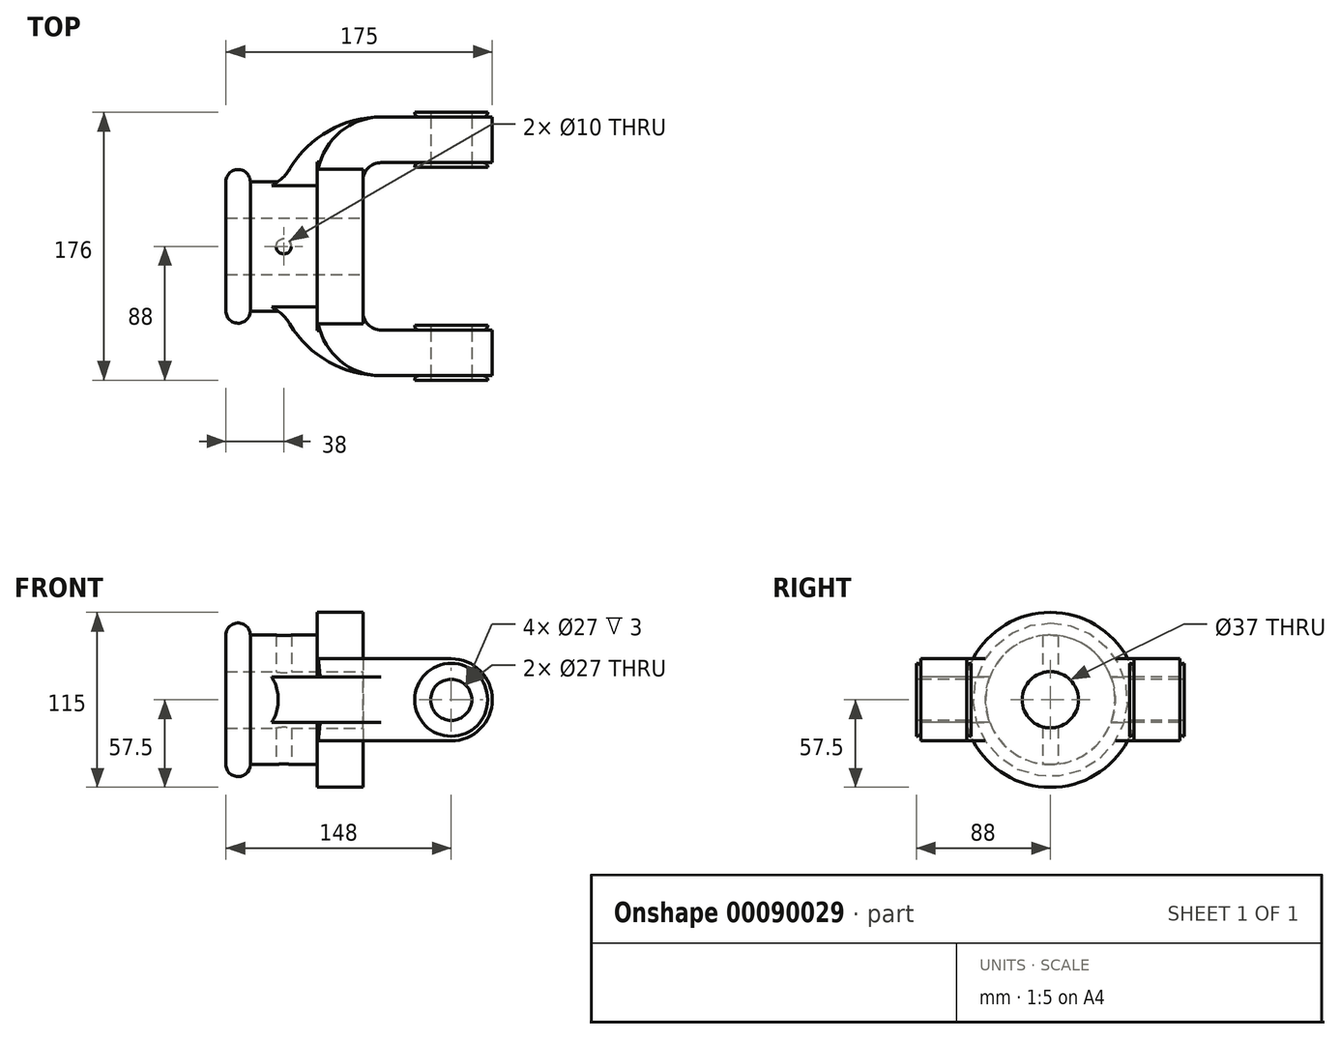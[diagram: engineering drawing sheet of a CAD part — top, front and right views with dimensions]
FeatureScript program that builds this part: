
annotation { "Feature Type Name" : "Feature", "Feature Type Description" : "" }
export const myFeature = defineFeature(function(context is Context, id is Id, definition is map)
    precondition{}
    {
        {
            var Q0;
            Q0=qCreatedBy(makeId("Top.planeOp"),FACE);
            var sketch = newSketch(context, id + "F0", { "sketchPlane" : qUnion([Q0])});
            skLineSegment(sketch, "E0", {"start": v(-90, 0) * mm, "end": v(85, 0) * mm, "construction": true});
            skLineSegment(sketch, "E1", {"start": v(0, 0) * mm, "end": v(0, 43) * mm});
            skLineSegment(sketch, "E2", {"start": v(12, 55) * mm, "end": v(85, 55) * mm});
            skLineSegment(sketch, "E3", {"start": v(85, 55) * mm, "end": v(85, 85) * mm});
            skPoint(sketch, "E4.visualSharp", {"position": v(0, 55) * mm});
            skArc(sketch, "E4.filletArc", {"start": v(12, 55) * mm, "mid": v(3.51, 51.49) * mm, "end": v(0, 43) * mm});
            skLineSegment(sketch, "E5.0", {"start": v(12, 85) * mm, "end": v(85, 85) * mm});
            skArc(sketch, "E5.1", {"start": v(12, 85) * mm, "mid": v(-17.7, 72.7) * mm, "end": v(-30, 43) * mm});
            skLineSegment(sketch, "E5.2", {"start": v(-30, 0) * mm, "end": v(-30, 43) * mm});
            skLineSegment(sketch, "E6.MirrorCS", {"start": v(0, 0) * mm, "end": v(0, -43) * mm});
            skLineSegment(sketch, "E7.MirrorCS", {"start": v(-30, 0) * mm, "end": v(-30, -43) * mm});
            skArc(sketch, "E8.MirrorCS", {"start": v(12, -85) * mm, "mid": v(-17.7, -72.7) * mm, "end": v(-30, -43) * mm});
            skArc(sketch, "E9.MirrorCS", {"start": v(12, -55) * mm, "mid": v(3.51, -51.49) * mm, "end": v(0, -43) * mm});
            skLineSegment(sketch, "E10.MirrorCS", {"start": v(12, -55) * mm, "end": v(85, -55) * mm});
            skLineSegment(sketch, "E11.MirrorCS", {"start": v(12, -85) * mm, "end": v(85, -85) * mm});
            skLineSegment(sketch, "E12.MirrorCS", {"start": v(85, -55) * mm, "end": v(85, -85) * mm});
            skArc(sketch, "E13", {"start": v(12, 85) * mm, "mid": v(-22.47, 75.93) * mm, "end": v(-48, 51.06) * mm});
            skLineSegment(sketch, "E14", {"start": v(-74, 42.5) * mm, "end": v(-30, 42.5) * mm});
            skLineSegment(sketch, "E15", {"start": v(-90, 42.5) * mm, "end": v(-90, 0) * mm});
            skArc(sketch, "E16", {"start": v(-74, 42.5) * mm, "mid": v(-82, 50.5) * mm, "end": v(-90, 42.5) * mm});
            skArc(sketch, "E17", {"start": v(-60, 39.83) * mm, "mid": v(-53.22, 44.6) * mm, "end": v(-48, 51.06) * mm});
            skLineSegment(sketch, "E18", {"start": v(-90, 0) * mm, "end": v(-30, 0) * mm});
            skArc(sketch, "E19.MirrorCS", {"start": v(12, -85) * mm, "mid": v(-22.47, -75.93) * mm, "end": v(-48, -51.06) * mm});
            skArc(sketch, "E20.MirrorCS", {"start": v(-60, -39.83) * mm, "mid": v(-53.22, -44.6) * mm, "end": v(-48, -51.06) * mm});
            skLineSegment(sketch, "E21", {"start": v(-60, 39.83) * mm, "end": v(-60, -39.83) * mm});
            skSolve(sketch);
        }
        {
            var Q0;
            {var subQ1=sQuery(id+"F0.wireOp",EDGE,"E7.MirrorCS");Q0=makeQuery(id+"F0.imprint","IMPRINT",FACE,{"disambiguationData":[TD([[makeQuery(id+"F0.imprint","IMPRINT",EDGE,{"derivedFrom":subQ1}),-1.0]])]});}
            var Q1;
            {var subQ1=sQuery(id+"F0.wireOp",EDGE,"E5.2");var subQ5=sQuery(id+"F0.wireOp",EDGE,"E14");var subQ6=makeQuery(id+"F0.imprint","INTERSECT",VERTEX,{"derivedFrom":[subQ1,subQ5]});Q1=makeQuery(id+"F0.imprint","IMPRINT",FACE,{"disambiguationData":[TD([[makeQuery(id+"F0.imprint","IMPRINT",EDGE,{"disambiguationData":[TD([[subQ6,1.0]])],"derivedFrom":subQ5}),-1.0]])]});}
            var Q2;
            {var subQ6=sQuery(id+"F0.wireOp",EDGE,"E5.1");Q2=makeQuery(id+"F0.imprint","IMPRINT",FACE,{"disambiguationData":[TD([[makeQuery(id+"F0.imprint","IMPRINT",EDGE,{"derivedFrom":subQ6}),-1.0]])]});}
            extrude(context, id + "F1", {"entities" : qUnion([Q0, Q1, Q2]), "depth" : 30 * mm, "symmetric" : true});
        }
        {
            var Q0;
            {var subQ6=sQuery(id+"F0.wireOp",EDGE,"E15");Q0=makeQuery(id+"F0.imprint","IMPRINT",FACE,{"disambiguationData":[TD([[makeQuery(id+"F0.imprint","IMPRINT",EDGE,{"derivedFrom":subQ6}),1.0]])]});}
            var Q1;
            {var subQ1=sQuery(id+"F0.wireOp",EDGE,"E5.2");var subQ5=sQuery(id+"F0.wireOp",EDGE,"E14");var subQ6=makeQuery(id+"F0.imprint","INTERSECT",VERTEX,{"derivedFrom":[subQ1,subQ5]});Q1=makeQuery(id+"F0.imprint","IMPRINT",FACE,{"disambiguationData":[TD([[makeQuery(id+"F0.imprint","IMPRINT",EDGE,{"disambiguationData":[TD([[subQ6,1.0]])],"derivedFrom":subQ5}),-1.0]])]});}
            var Q2;
            Q2=sQuery(id+"F0.wireOp",EDGE,"E18");
            revolve(context, id + "F2", {"operationType" : NewBodyOperationType.ADD, "entities" : qUnion([Q0, Q1]), "axis" : qUnion([Q2]), "revolveType" : RevolveType.FULL});
        }
        {
            var Q0;
            Q0=makeQuery(id+"F0.imprint","IMPRINT",FACE,{"disambiguationData":[TD([[makeQuery(id+"F0.imprint","IMPRINT",EDGE,{"derivedFrom":sQuery(id+"F0.wireOp",EDGE,"E1")}),1.0]])]});
            extrude(context, id + "F3", {"entities" : qUnion([Q0]), "operationType" : NewBodyOperationType.ADD, "depth" : 54 * mm, "symmetric" : true});
        }
        {
            var Q0;
            Q0=qCreatedBy(makeId("Right.planeOp"),FACE);
            var sketch = newSketch(context, id + "F4", { "sketchPlane" : qUnion([Q0])});
            skCircle(sketch, "E22", {"center": v(0, 0) * mm, "radius": 57.5 * mm});
            skSolve(sketch);
        }
        {
            var Q0;
            Q0=makeQuery(id+"F4.imprint","IMPRINT",FACE,{"disambiguationData":[TD([[makeQuery(id+"F4.imprint","IMPRINT",EDGE,{"derivedFrom":sQuery(id+"F4.wireOp",EDGE,"E22")}),1.0]])]});
            extrude(context, id + "F5", {"entities" : qUnion([Q0]), "operationType" : NewBodyOperationType.ADD, "oppositeDirection" : true, "depth" : 30 * mm});
        }
        {
            var Q0;
            Q0=makeQuery(id+"F3.opExtrude","CAP_EDGE",EDGE,{"disambiguationData":[OSD([sQuery(id+"F0.wireOp",EDGE,"E12.MirrorCS")])],"isStart":false});
            var Q1;
            Q1=makeQuery(id+"F3.opExtrude","CAP_EDGE",EDGE,{"disambiguationData":[OSD([sQuery(id+"F0.wireOp",EDGE,"E12.MirrorCS")])],"isStart":true});
            var Q2;
            Q2=makeQuery(id+"F3.opExtrude","CAP_EDGE",EDGE,{"disambiguationData":[OSD([sQuery(id+"F0.wireOp",EDGE,"E3")])],"isStart":false});
            var Q3;
            Q3=makeQuery(id+"F3.opExtrude","CAP_EDGE",EDGE,{"disambiguationData":[OSD([sQuery(id+"F0.wireOp",EDGE,"E3")])],"isStart":true});
            fillet(context, id + "F6", {"entities" : qUnion([Q0, Q1, Q2, Q3]), "radius" : 27 * mm, "tangentPropagation" : true, "allowEdgeOverflow" : false});
        }
        {
            var Q0;
            Q0=makeQuery(id+"F3.opExtrude","SWEPT_FACE",FACE,{"disambiguationData":[OSD([sQuery(id+"F0.wireOp",EDGE,"E11.MirrorCS")])]});
            var sketch = newSketch(context, id + "F7", { "sketchPlane" : qUnion([Q0])});
            skCircle(sketch, "E23", {"center": v(58, 0) * mm, "radius": 24 * mm});
            skSolve(sketch);
        }
        {
            var Q0;
            Q0=makeQuery(id+"F7.imprint","IMPRINT",FACE,{"disambiguationData":[TD([[makeQuery(id+"F7.imprint","IMPRINT",EDGE,{"derivedFrom":sQuery(id+"F7.wireOp",EDGE,"E23")}),1.0]])]});
            extrude(context, id + "F8", {"entities" : qUnion([Q0]), "depth" : 3 * mm});
        }
        {
            var Q0;
            Q0=makeQuery(id+"F8.opExtrude","SWEPT_BODY",BODY,{"disambiguationData":[OSD([sQuery(id+"F7.wireOp",EDGE,"E23")])]});
            var Q1;
            Q1=makeQuery(id+"F3.opExtrude","SWEPT_FACE",FACE,{"disambiguationData":[OSD([sQuery(id+"F0.wireOp",EDGE,"E10.MirrorCS")])]});
            transform(context, id + "F9", {"entities" : qUnion([Q0]), "transformType" : TransformType.TRANSLATION_DISTANCE, "transformDirection" : qUnion([Q1]), "distance" : 33 * mm, "makeCopy" : true});
        }
        {
            var Q0;
            Q0=makeQuery(id+"F8.opExtrude","SWEPT_BODY",BODY,{"disambiguationData":[OSD([sQuery(id+"F7.wireOp",EDGE,"E23")])]});
            var Q1;
            Q1=makeQuery(id+"F9.opPattern","COPY",BODY,{"derivedFrom":makeQuery(id+"F8.opExtrude","SWEPT_BODY",BODY,{"disambiguationData":[OSD([sQuery(id+"F7.wireOp",EDGE,"E23")])]}),"instanceName":"1"});
            var Q2;
            Q2=makeQuery(id+"F3.opExtrude","SWEPT_FACE",FACE,{"disambiguationData":[OSD([sQuery(id+"F0.wireOp",EDGE,"E5.0")])]});
            transform(context, id + "F10", {"entities" : qUnion([Q0, Q1]), "transformType" : TransformType.TRANSLATION_DISTANCE, "transformDirection" : qUnion([Q2]), "distance" : 140 * mm, "makeCopy" : true});
        }
        {
            var Q0;
            Q0=qCreatedBy(makeId("Front.planeOp"),FACE);
            var sketch = newSketch(context, id + "F11", { "sketchPlane" : qUnion([Q0])});
            skCircle(sketch, "E24", {"center": v(58, 0) * mm, "radius": 13.5 * mm});
            skSolve(sketch);
        }
        {
            var Q0;
            Q0=makeQuery(id+"F11.imprint","IMPRINT",FACE,{"disambiguationData":[TD([[makeQuery(id+"F11.imprint","IMPRINT",EDGE,{"derivedFrom":sQuery(id+"F11.wireOp",EDGE,"E24")}),1.0]])]});
            extrude(context, id + "F12", {"entities" : qUnion([Q0]), "operationType" : NewBodyOperationType.REMOVE, "oppositeDirection" : true, "depth" : 185 * mm, "symmetric" : true});
        }
        {
            var Q0;
            Q0=qCreatedBy(makeId("Right.planeOp"),FACE);
            var sketch = newSketch(context, id + "F13", { "sketchPlane" : qUnion([Q0])});
            skCircle(sketch, "E25", {"center": v(0, 0) * mm, "radius": 18.5 * mm});
            skSolve(sketch);
        }
        {
            var Q0;
            Q0=makeQuery(id+"F13.imprint","IMPRINT",FACE,{"disambiguationData":[TD([[makeQuery(id+"F13.imprint","IMPRINT",EDGE,{"derivedFrom":sQuery(id+"F13.wireOp",EDGE,"E25")}),1.0]])]});
            extrude(context, id + "F14", {"entities" : qUnion([Q0]), "operationType" : NewBodyOperationType.REMOVE, "endBound" : BoundingType.UP_TO_NEXT, "oppositeDirection" : true, "depth" : 25 * mm});
        }
        {
            var Q0;
            Q0=makeQuery(id+"F8.opExtrude","CAP_EDGE",EDGE,{"disambiguationData":[OSD([sQuery(id+"F7.wireOp",EDGE,"E23")])],"isStart":true});
            var Q1;
            Q1=makeQuery(id+"F10.opPattern","COPY",EDGE,{"derivedFrom":makeQuery(id+"F8.opExtrude","CAP_EDGE",EDGE,{"disambiguationData":[OSD([sQuery(id+"F7.wireOp",EDGE,"E23")])],"isStart":true}),"instanceName":"1"});
            var Q2;
            Q2=makeQuery(id+"F9.opPattern","COPY",EDGE,{"derivedFrom":makeQuery(id+"F8.opExtrude","CAP_EDGE",EDGE,{"disambiguationData":[OSD([sQuery(id+"F7.wireOp",EDGE,"E23")])],"isStart":false}),"instanceName":"1"});
            var Q3;
            Q3=makeQuery(id+"F10.opPattern","COPY",EDGE,{"derivedFrom":makeQuery(id+"F9.opPattern","COPY",EDGE,{"derivedFrom":makeQuery(id+"F8.opExtrude","CAP_EDGE",EDGE,{"disambiguationData":[OSD([sQuery(id+"F7.wireOp",EDGE,"E23")])],"isStart":false}),"instanceName":"1"}),"instanceName":"1"});
            fillet(context, id + "F15", {"entities" : qUnion([Q0, Q1, Q2, Q3]), "radius" : 3 * mm, "tangentPropagation" : true, "allowEdgeOverflow" : false});
        }
        {
            var Q0;
            Q0=qCreatedBy(makeId("Top.planeOp"),FACE);
            var sketch = newSketch(context, id + "F16", { "sketchPlane" : qUnion([Q0])});
            skCircle(sketch, "E26", {"center": v(-52, 0) * mm, "radius": 5 * mm});
            skSolve(sketch);
        }
        {
            var Q0;
            Q0 = qSketchRegion(id + "F16", true);
            extrude(context, id + "F17", {"entities" : qUnion([Q0]), "operationType" : NewBodyOperationType.REMOVE, "depth" : 100 * mm, "symmetric" : true});
        }
    });
